# Revit family: sh-2612
name_source: partatom
category: Lighting Fixtures
revit_build: Autodesk Revit 2017 (Build: 20160225_1515(x64)
units: mm (PartAtom-declared; Revit-internal decimal feet)

## family parameters
Always vertical = Yes
Cut with Voids When Loaded = No
Host = Ceiling
Light Source = Yes
OmniClass Number = 23.80.70.11
OmniClass Title = Luminaries for Internal Lighting
Part Type = Normal
Room Calculation Point = No
Round Connector Dimension = Use Diameter
Shared = No

## types (1)
- SH-2612(white body-E27)
    Body Material = ABS
    Body color = white body
    Color Filter = 16777215
    Default Elevation = 0 cm
    Diameter = 27 cm
    Dimming Lamp Color Temperature Shift = <None>
    Emit Shape Visible in Rendering = No
    Emit from Circle Diameter = 20 cm
    Height = 9 cm
    IP = 4X
    Lamp = E27
    Manufacturer = SHOA
    Model = SH-2612
    Number of Lamps = 1
    Photometric Web File = SH 2612.ies
    Tilt Angle = 90.00°
    URL = https://www.shoaco.com
    Voltage/Frequency = 230V-50HZ
    Wattage. = 15w
    instalation = Surface Mounted
    website = www.shoaco.com

## geometry (parser evidence)
native form markers: Sweep x3
no freeform markers — native parametric forms only
